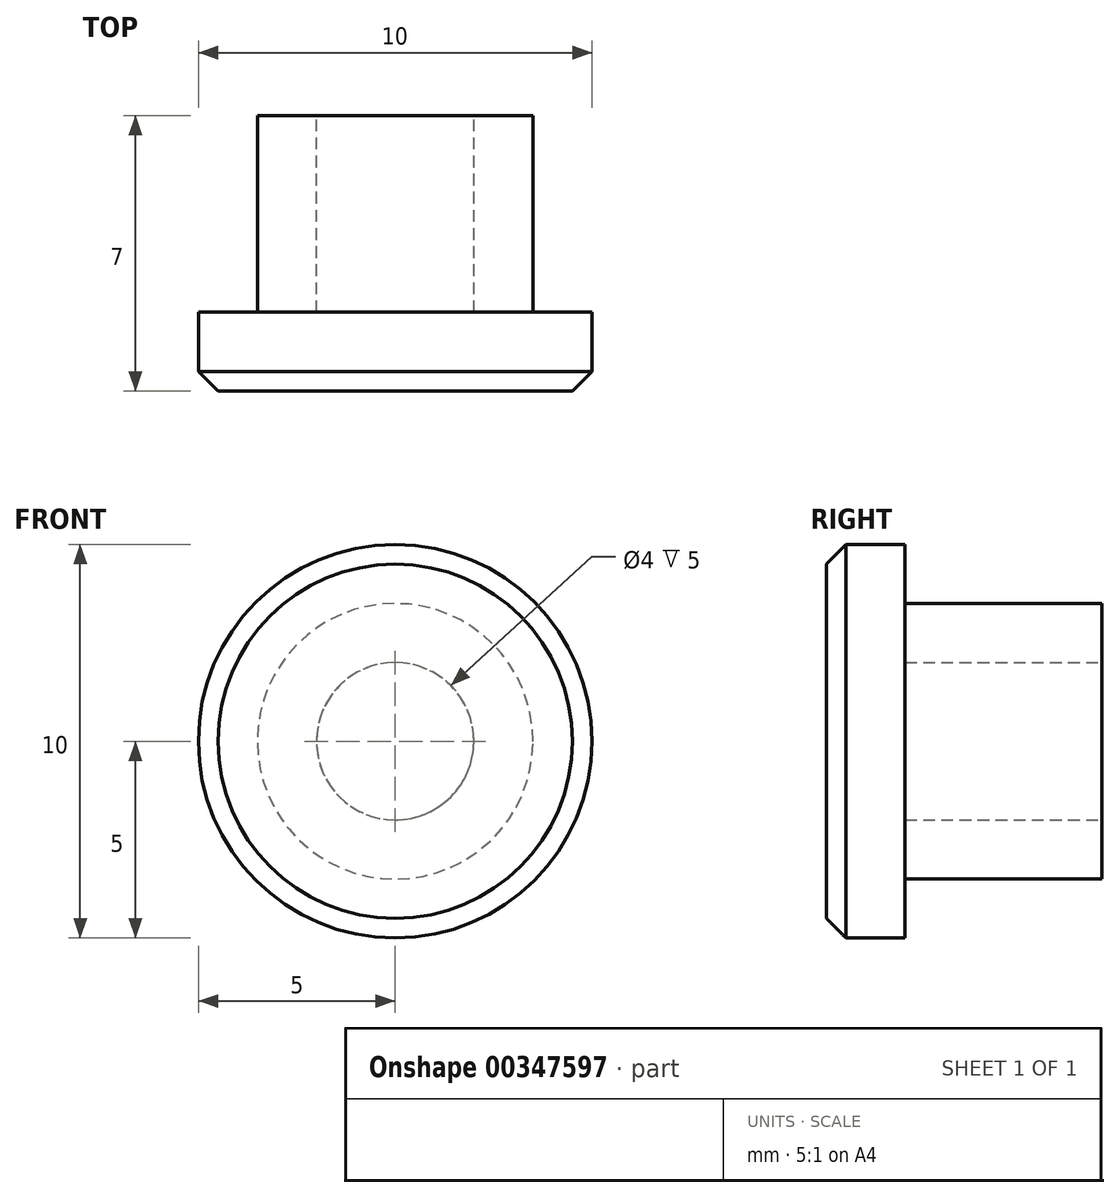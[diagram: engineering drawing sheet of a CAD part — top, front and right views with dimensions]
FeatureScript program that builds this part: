
annotation { "Feature Type Name" : "Feature", "Feature Type Description" : "" }
export const myFeature = defineFeature(function(context is Context, id is Id, definition is map)
    precondition{}
    {
        {
            var Q0;
            Q0=qCreatedBy(makeId("Front.planeOp"),FACE);
            var sketch = newSketch(context, id + "F0", { "sketchPlane" : qUnion([Q0])});
            skCircle(sketch, "E0", {"center": v(0, 0) * mm, "radius": 3.5 * mm});
            skSolve(sketch);
        }
        {
            var Q0;
            Q0 = qSketchRegion(id + "F0", true);
            extrude(context, id + "F1", {"entities" : qUnion([Q0]), "depth" : 5 * mm});
        }
        {
            var Q0;
            Q0=makeQuery(id+"F1.opExtrude","CAP_FACE",FACE,{"disambiguationData":[OSD([sQuery(id+"F0.wireOp",EDGE,"E0")])],"isStart":false});
            var sketch = newSketch(context, id + "F2", { "sketchPlane" : qUnion([Q0])});
            skCircle(sketch, "E1", {"center": v(0, 0) * mm, "radius": 5 * mm});
            skSolve(sketch);
        }
        {
            var Q0;
            Q0=makeQuery(id+"F2.imprint","IMPRINT",FACE,{"disambiguationData":[TD([[makeQuery(id+"F2.imprint","IMPRINT",EDGE,{"derivedFrom":sQuery(id+"F2.wireOp",EDGE,"E1")}),1.0]])]});
            var Q1;
            Q1=makeQuery(id+"F2.imprint","IMPRINT",FACE,{"disambiguationData":[TD([[makeQuery(id+"F2.imprint","IMPRINT",EDGE,{"derivedFrom":makeQuery(id+"F1.opExtrude","CAP_EDGE",EDGE,{"disambiguationData":[OSD([sQuery(id+"F0.wireOp",EDGE,"E0")])],"isStart":false})}),1.0]])]});
            extrude(context, id + "F3", {"entities" : qUnion([Q0, Q1]), "operationType" : NewBodyOperationType.ADD, "depth" : 2 * mm});
        }
        {
            var Q0;
            Q0=makeQuery(id+"F1.opExtrude","CAP_FACE",FACE,{"disambiguationData":[OSD([sQuery(id+"F0.wireOp",EDGE,"E0")])],"isStart":true});
            var sketch = newSketch(context, id + "F4", { "sketchPlane" : qUnion([Q0])});
            skCircle(sketch, "E2", {"center": v(0, 0) * mm, "radius": 2 * mm});
            skSolve(sketch);
        }
        {
            var Q0;
            Q0=makeQuery(id+"F4.imprint","IMPRINT",FACE,{"disambiguationData":[TD([[makeQuery(id+"F4.imprint","IMPRINT",EDGE,{"derivedFrom":sQuery(id+"F4.wireOp",EDGE,"E2")}),1.0]])]});
            var Q1;
            Q1=makeQuery(id+"F3.opExtrude","CAP_FACE",FACE,{"disambiguationData":[OSD([sQuery(id+"F2.wireOp",EDGE,"E1")])],"isStart":true});
            extrude(context, id + "F5", {"entities" : qUnion([Q0]), "operationType" : NewBodyOperationType.REMOVE, "endBound" : BoundingType.UP_TO_SURFACE, "oppositeDirection" : true, "endBoundEntityFace" : qUnion([Q1]), "depth" : 25 * mm});
        }
        {
            var Q0;
            Q0=makeQuery(id+"F3.opExtrude","CAP_EDGE",EDGE,{"disambiguationData":[OSD([sQuery(id+"F2.wireOp",EDGE,"E1")])],"isStart":false});
            chamfer(context, id + "F6", {"entities" : qUnion([Q0]), "width" : .5 * mm, "tangentPropagation" : true});
        }
    });
